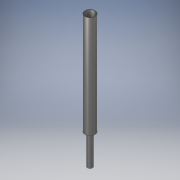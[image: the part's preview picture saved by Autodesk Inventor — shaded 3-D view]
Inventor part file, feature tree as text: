
AUTODESK INVENTOR PART (.ipt)
format: ipt  version: 2018 (Build 220112000, 112)  size: 112,640 bytes
history: native  units: in
note: dims shown in document units (in); Inventor stores cm internally (conversion verified against a paired STEP export)
features: extrude x3, sketch x3
ambient origin geometry x8: Origin, YZ Plane, XZ Plane, XY Plane, X Axis, Y Axis, Z Axis, Center Point
bodies: Solid1 (feature_tree)
feature tree (6):
  extrude  "Extrusion1"  Depth=0.95in
  extrude  "Extrusion2"  Depth=0.5in
  extrude  "Extrusion3"  Depth=0.5in
  sketch  "Sketch1"  dims[d0=1.0in d1=0.95in]
  sketch  "Sketch2"  dims[d2=10.0in d3=0.0in d4=0.5in]
  sketch  "Sketch3"  dims[d5=0.05in d6=0.0in d7=0.5in d8=0.44in d9=3.0in d10=0.0in]
